FCSTD DOCUMENT  (FreeCAD 0.15R4671 (Git))
Label: Robot1cTrikeAssembly
License: All rights reserved
LicenseURL: http://en.wikipedia.org/wiki/All_rights_reserved
objects: Part::Part2DObjectPython×11, App::DocumentObjectGroup×1
note: 11 computed .brp shape members not serialized (recipe doc carries the construction recipe); baked Part::Feature solids carry a one-line shape summary decoded from their .brp

FEATURE [Part::Part2DObjectPython] DWire  label="Trike Side 1"  # Draft 2D object (typed FeaturePython)
  ChamferSize = 0
  Closed = true
  End = (-35.3675,56.5727,0)
  FilletRadius = 0
  Length = 102.8
  MakeFace = false
  Placement = pos=(57.6325,126.573,0) rot=(0,0,1;0rad)
  Points = (12) [(-93,-40,0),(-90.8,-40,0),(-90.8,-37.3,0),(-79.2,-37.3,0),(-79.2,-40,0),(-77,-40,0),(-77,-70,0),(-79.2,-70,0),(-79.2,-72.7,0),(-90.8,-72.7,0),(-90.8,-70,0),(-93,-70,0)]
  Start = (-35.3675,86.5727,0)
FEATURE [Part::Part2DObjectPython] DWire001  label="Trike Side 2"  # Draft 2D object (typed FeaturePython)
  ChamferSize = 0
  Closed = true
  End = (-13.4612,56.2079,0)
  FilletRadius = 0
  Length = 102.8
  MakeFace = false
  Placement = pos=(79.5388,126.208,0) rot=(0,0,1;0rad)
  Points = (12) [(-93,-40,0),(-90.8,-40,0),(-90.8,-37.3,0),(-79.2,-37.3,0),(-79.2,-40,0),(-77,-40,0),(-77,-70,0),(-79.2,-70,0),(-79.2,-72.7,0),(-90.8,-72.7,0),(-90.8,-70,0),(-93,-70,0)]
  Start = (-13.4612,86.2079,0)
FEATURE [Part::Part2DObjectPython] Rectangle  label="Trike Base Rectangle"  # Draft 2D object (typed FeaturePython)
  ChamferSize = 0
  FilletRadius = 0
  Height = -20
  Length = -48
  MakeFace = false
  Placement = pos=(-40.1983,88.9919,0) rot=(0,0,1;0rad)
FEATURE [Part::Part2DObjectPython] Circle  label="Front Wheel Hole Right"  # Draft 2D object (typed FeaturePython)
  FirstAngle = 0
  LastAngle = 0
  MakeFace = false
  Placement = pos=(-56.8483,78.9919,0) rot=(0,0,1;0rad)
  Radius = 1.13
FEATURE [Part::Part2DObjectPython] Circle001  label="Front Wheel Hole Left"  # Draft 2D object (typed FeaturePython)
  FirstAngle = 0
  LastAngle = 0
  MakeFace = false
  Placement = pos=(-71.5483,78.9919,0) rot=(0,0,1;0rad)
  Radius = 1.13
FEATURE [Part::Part2DObjectPython] Rectangle001  label="Right Trike Slot001"  # Draft 2D object (typed FeaturePython)
  ChamferSize = 0
  FilletRadius = 0
  Height = -12
  Length = 3
  MakeFace = false
  Placement = pos=(-47.1983,84.9919,0) rot=(0,0,1;0rad)
FEATURE [Part::Part2DObjectPython] Rectangle002  label="Left Trike Slot001"  # Draft 2D object (typed FeaturePython)
  ChamferSize = 0
  FilletRadius = 0
  Height = -12
  Length = 3
  MakeFace = false
  Placement = pos=(-84.1983,84.9919,0) rot=(0,0,1;0rad)
FEATURE [Part::Part2DObjectPython] DWire002  label="Brace 1"  # Draft 2D object (typed FeaturePython)
  ChamferSize = 0
  Closed = true
  End = (-69.4838,49.3669,0)
  FilletRadius = 0
  Length = 34.1421
  MakeFace = false
  Placement = pos=(-9.48383,89.3669,0) rot=(0,0,1;0rad)
  Points = (3) [(-70,-30,0),(-70,-40,0),(-60,-40,0)]
  Start = (-79.4838,59.3669,0)
FEATURE [Part::Part2DObjectPython] DWire003  label="Brace 2"  # Draft 2D object (typed FeaturePython)
  ChamferSize = 0
  Closed = true
  End = (-50.007,34.4116,0)
  FilletRadius = 0
  Length = 34.1421
  MakeFace = false
  Placement = pos=(9.99302,74.4116,0) rot=(0,0,1;0rad)
  Points = (3) [(-70,-30,0),(-70,-40,0),(-60,-40,0)]
  Start = (-60.007,44.4116,0)
FEATURE [Part::Part2DObjectPython] DWire004  label="Brace 3"  # Draft 2D object (typed FeaturePython)
  ChamferSize = 0
  Closed = true
  End = (-50.9876,49.1191,0)
  FilletRadius = 0
  Length = 34.1421
  MakeFace = false
  Placement = pos=(9.01241,89.1191,0) rot=(0,0,1;0rad)
  Points = (3) [(-70,-30,0),(-70,-40,0),(-60,-40,0)]
  Start = (-60.9876,59.1191,0)
FEATURE [Part::Part2DObjectPython] DWire005  label="Brace 4"  # Draft 2D object (typed FeaturePython)
  ChamferSize = 0
  Closed = true
  End = (-69.327,34.1638,0)
  FilletRadius = 0
  Length = 34.1421
  MakeFace = false
  Placement = pos=(-9.32701,74.1638,0) rot=(0,0,1;0rad)
  Points = (3) [(-70,-30,0),(-70,-40,0),(-60,-40,0)]
  Start = (-79.327,44.1638,0)
FEATURE [App::DocumentObjectGroup] Group  label="Trike Base Plate"
  Group = -> [Rectangle,Circle,Circle001,Rectangle001,Rectangle002]
